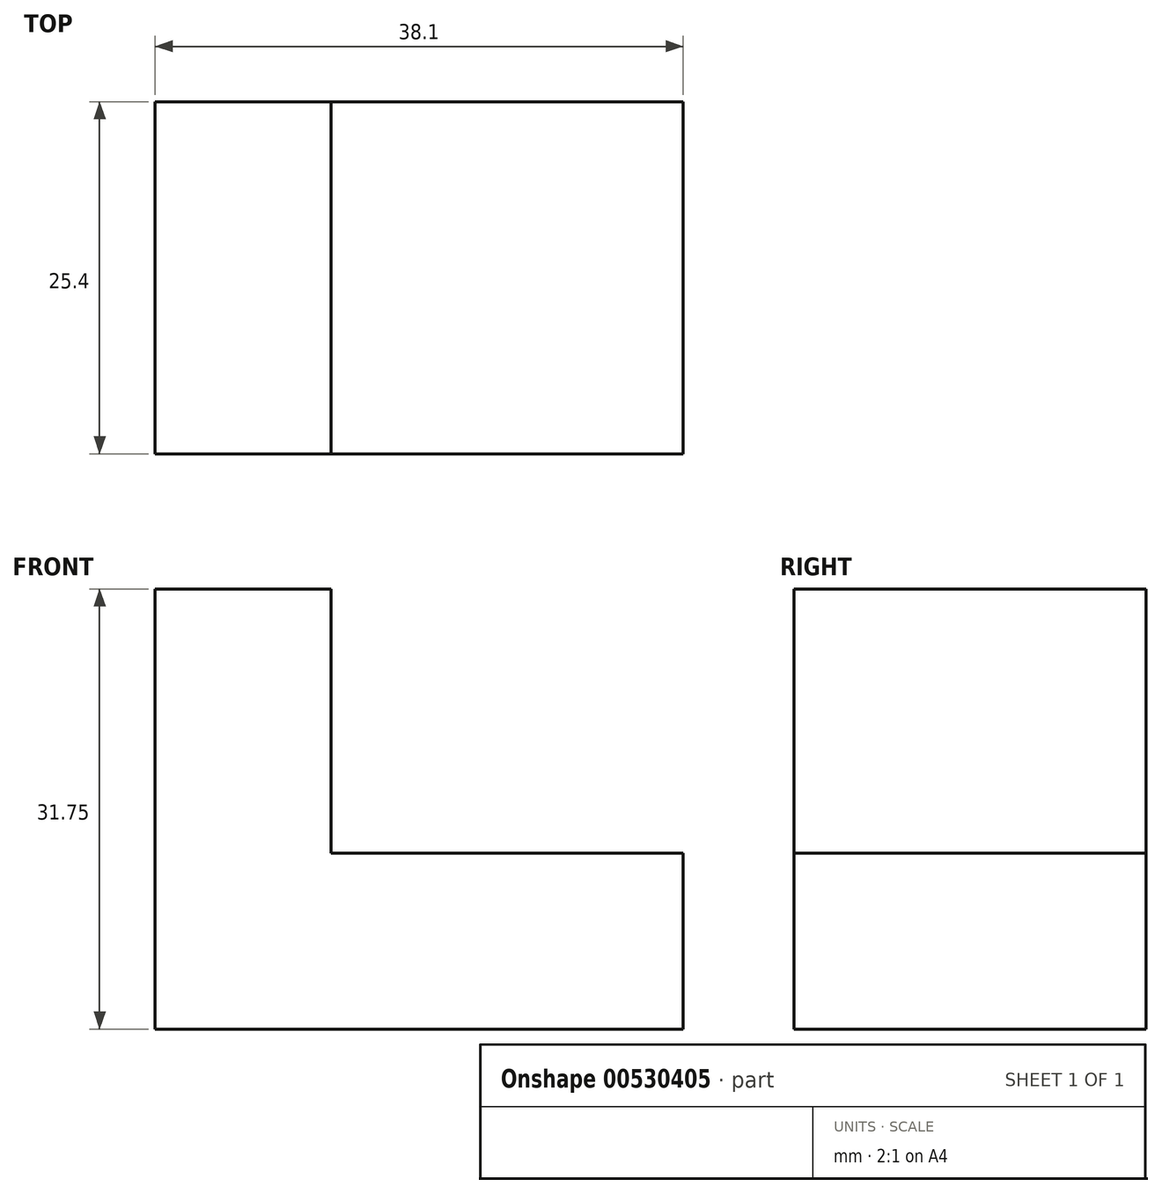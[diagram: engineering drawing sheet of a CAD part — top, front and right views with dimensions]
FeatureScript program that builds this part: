
annotation { "Feature Type Name" : "Feature", "Feature Type Description" : "" }
export const myFeature = defineFeature(function(context is Context, id is Id, definition is map)
    precondition{}
    {
        {
            var Q0;
            Q0=qCreatedBy(makeId("Front.planeOp"),FACE);
            var sketch = newSketch(context, id + "F0", { "sketchPlane" : qUnion([Q0])});
            skLineSegment(sketch, "E0", {"start": v(-112.32, 31.75) * mm, "end": v(-112.32, 0) * mm});
            skLineSegment(sketch, "E1", {"start": v(-74.22, 0) * mm, "end": v(-74.22, 12.7) * mm});
            skLineSegment(sketch, "E2", {"start": v(-74.22, 12.7) * mm, "end": v(-99.62, 12.7) * mm});
            skLineSegment(sketch, "E3", {"start": v(-112.32, 31.75) * mm, "end": v(-99.62, 31.75) * mm});
            skLineSegment(sketch, "E4", {"start": v(-99.62, 31.75) * mm, "end": v(-99.62, 12.7) * mm});
            skLineSegment(sketch, "E5", {"start": v(-112.32, 0) * mm, "end": v(-74.22, 0) * mm});
            skLineSegment(sketch, "E6", {"start": v(-99.62, 12.7) * mm, "end": v(-99.62, 12.7) * mm});
            skSolve(sketch);
        }
        {
            var Q0;
            Q0=makeQuery(id+"F0.imprint","IMPRINT",FACE,{"disambiguationData":[TD([[makeQuery(id+"F0.imprint","IMPRINT",EDGE,{"derivedFrom":sQuery(id+"F0.wireOp",EDGE,"E0")}),1.0]])]});
            extrude(context, id + "F1", {"entities" : qUnion([Q0]), "depth" : 25.4 * mm, "offsetDistance" : 25.4 * mm});
        }
    });
